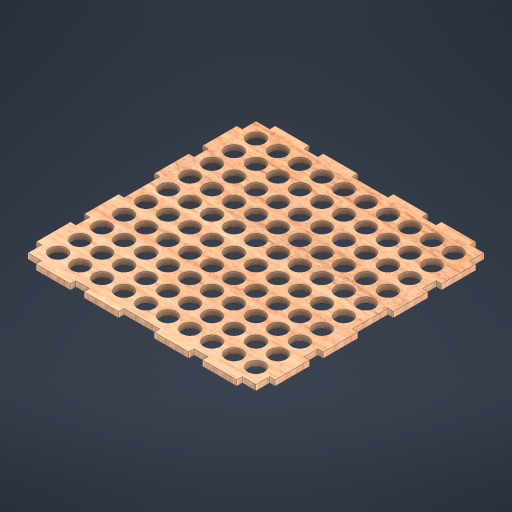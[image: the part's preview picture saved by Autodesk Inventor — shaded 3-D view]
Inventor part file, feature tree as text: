
AUTODESK INVENTOR PART (.ipt)
format: ipt  version: 2024.1 (Build 281209000, 209)  size: 620,544 bytes
history: native  units: mm
features: extrude x1, sketch x1
ambient origin geometry x8: Origin, YZ Plane, XZ Plane, XY Plane, X Axis, Y Axis, Z Axis, Center Point
bodies: Solid1 (feature_tree)
feature tree (2):
  extrude  "Extrusion1"  Depth=100.0mm
  sketch  "Sketch1"  dims[d0=12.0mm d1=100.0mm d3=16.0mm d4=100.0mm d6=16.0mm d9=5.0mm d10=5.0mm d11=4.0mm d12=4.0mm d13=10.0mm d14=10.0mm d15=25.0mm d16=4.0mm d17=25.0mm d18=10.0mm d19=25.0mm d20=10.0mm d21=25.0mm d22=4.0mm d23=40.0mm d25=360.0deg d27=4.0mm d28=0.0mm]
